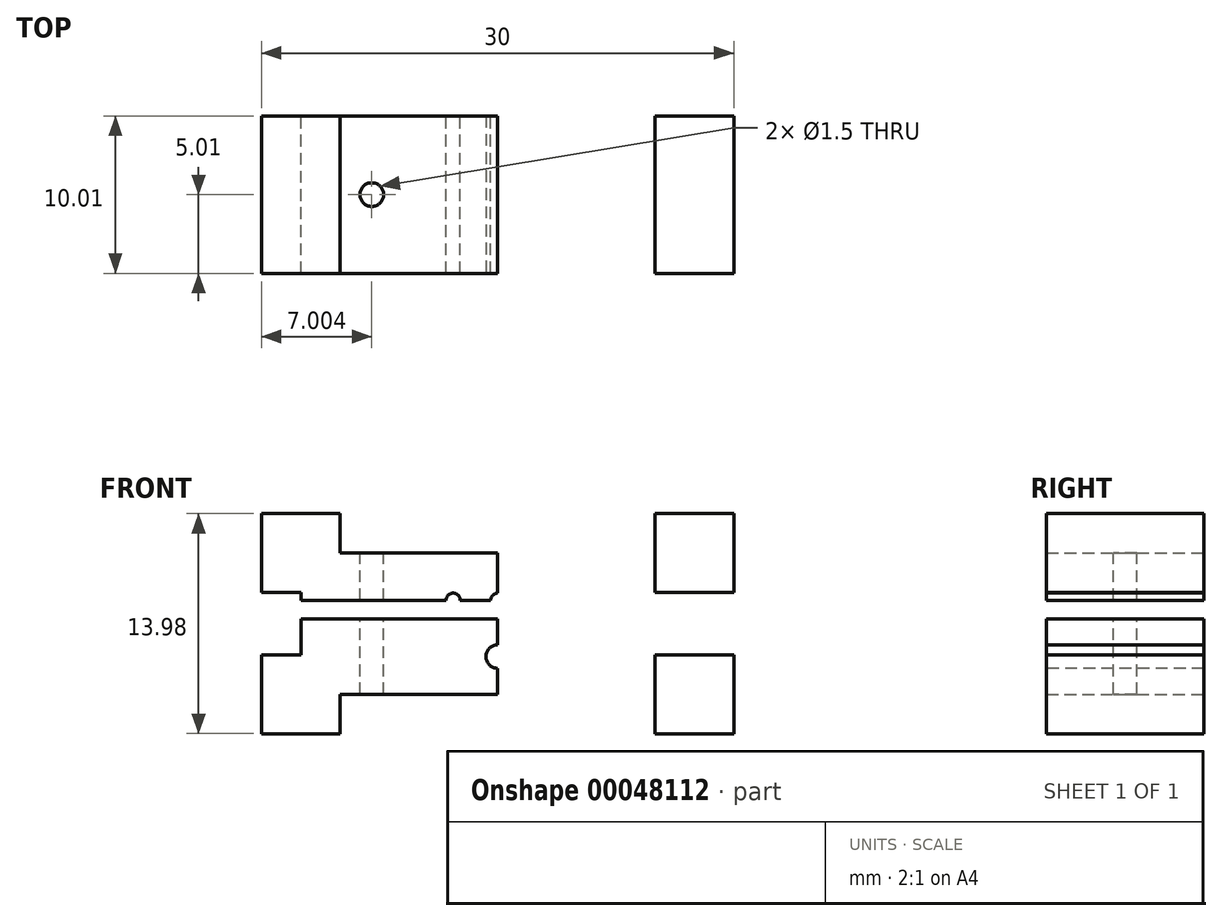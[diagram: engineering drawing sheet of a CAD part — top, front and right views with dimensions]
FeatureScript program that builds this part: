
annotation { "Feature Type Name" : "Feature", "Feature Type Description" : "" }
export const myFeature = defineFeature(function(context is Context, id is Id, definition is map)
    precondition{}
    {
        {
            var Q0;
            Q0=qCreatedBy(makeId("Front.planeOp"),FACE);
            var sketch = newSketch(context, id + "F0", { "sketchPlane" : qUnion([Q0])});
            skLineSegment(sketch, "E0.bottom", {"start": v(-11.09, -0.38) * mm, "end": v(1.41, -0.38) * mm});
            skLineSegment(sketch, "E0.top", {"start": v(-11.09, -5.18) * mm, "end": v(1.41, -5.18) * mm});
            skLineSegment(sketch, "E0.left", {"start": v(-11.09, -0.38) * mm, "end": v(-11.09, -5.18) * mm});
            skLineSegment(sketch, "E0.right", {"start": v(1.41, -0.38) * mm, "end": v(1.41, -5.18) * mm});
            skLineSegment(sketch, "E1.rect.bottom", {"start": v(-8.59, -2.68) * mm, "end": v(-13.59, -2.68) * mm});
            skLineSegment(sketch, "E1.rect.top", {"start": v(-8.59, -7.68) * mm, "end": v(-13.59, -7.68) * mm});
            skLineSegment(sketch, "E1.rect.left", {"start": v(-8.59, -2.68) * mm, "end": v(-8.59, -7.68) * mm});
            skLineSegment(sketch, "E1.rect.right", {"start": v(-13.59, -2.68) * mm, "end": v(-13.59, -7.68) * mm});
            skPoint(sketch, "E1.rect.middle", {"position": v(-11.09, -5.18) * mm});
            skLineSegment(sketch, "E2.bottom", {"start": v(-11.09, 0.8) * mm, "end": v(1.41, 0.8) * mm});
            skLineSegment(sketch, "E2.top", {"start": v(-11.09, 3.8) * mm, "end": v(1.41, 3.8) * mm});
            skLineSegment(sketch, "E2.left", {"start": v(-11.09, 0.8) * mm, "end": v(-11.09, 3.8) * mm});
            skLineSegment(sketch, "E2.right", {"start": v(1.41, 0.8) * mm, "end": v(1.41, 3.8) * mm});
            skLineSegment(sketch, "E3.rect.bottom", {"start": v(-8.59, 6.3) * mm, "end": v(-13.59, 6.3) * mm});
            skLineSegment(sketch, "E3.rect.top", {"start": v(-8.59, 1.3) * mm, "end": v(-13.59, 1.3) * mm});
            skLineSegment(sketch, "E3.rect.left", {"start": v(-8.59, 6.3) * mm, "end": v(-8.59, 1.3) * mm});
            skLineSegment(sketch, "E3.rect.right", {"start": v(-13.59, 6.3) * mm, "end": v(-13.59, 1.3) * mm});
            skPoint(sketch, "E3.rect.middle", {"position": v(-11.09, 3.8) * mm});
            skCircle(sketch, "E4", {"center": v(1.41, 0.8) * mm, "radius": 0.45 * mm});
            skCircle(sketch, "E5.MirrorC", {"center": v(-1.41, 0.8) * mm, "radius": 0.45 * mm});
            skCircle(sketch, "E6.MirrorC", {"center": v(4.24, 0.8) * mm, "radius": 0.45 * mm});
            skPoint(sketch, "E7.MirrorP", {"position": v(13.91, -5.18) * mm});
            skLineSegment(sketch, "E8.MirrorCS", {"start": v(11.41, -7.68) * mm, "end": v(16.41, -7.68) * mm});
            skLineSegment(sketch, "E9.MirrorCS", {"start": v(11.41, -2.68) * mm, "end": v(16.41, -2.68) * mm});
            skLineSegment(sketch, "E10.MirrorCS", {"start": v(11.41, 6.3) * mm, "end": v(11.41, 1.3) * mm});
            skLineSegment(sketch, "E11.MirrorCS", {"start": v(16.41, -2.68) * mm, "end": v(16.41, -7.68) * mm});
            skPoint(sketch, "E12.MirrorP", {"position": v(13.91, 3.8) * mm});
            skLineSegment(sketch, "E13.MirrorCS", {"start": v(11.41, 6.3) * mm, "end": v(16.41, 6.3) * mm});
            skLineSegment(sketch, "E14.MirrorCS", {"start": v(13.91, -0.38) * mm, "end": v(1.41, -0.38) * mm});
            skLineSegment(sketch, "E15.MirrorCS", {"start": v(13.91, -0.38) * mm, "end": v(13.91, -5.18) * mm});
            skLineSegment(sketch, "E16.MirrorCS", {"start": v(13.91, -5.18) * mm, "end": v(1.41, -5.18) * mm});
            skLineSegment(sketch, "E17.MirrorCS", {"start": v(16.41, 6.3) * mm, "end": v(16.41, 1.3) * mm});
            skLineSegment(sketch, "E18.MirrorCS", {"start": v(13.91, 3.8) * mm, "end": v(1.41, 3.8) * mm});
            skLineSegment(sketch, "E19.MirrorCS", {"start": v(13.91, 0.8) * mm, "end": v(1.41, 0.8) * mm});
            skLineSegment(sketch, "E20.MirrorCS", {"start": v(11.41, 1.3) * mm, "end": v(16.41, 1.3) * mm});
            skLineSegment(sketch, "E21.MirrorCS", {"start": v(13.91, 0.8) * mm, "end": v(13.91, 3.8) * mm});
            skLineSegment(sketch, "E22.MirrorCS", {"start": v(11.41, -2.68) * mm, "end": v(11.41, -7.68) * mm});
            skPoint(sketch, "E23", {"position": v(1.41, -2.78) * mm});
            skSolve(sketch);
        }
        {
            var Q0;
            {var subQ0=sQuery(id+"F0.wireOp",EDGE,"E2.left");var subQ1=sQuery(id+"F0.wireOp",EDGE,"E2.bottom");var subQ2=makeQuery(id+"F0.imprint","INTERSECT",VERTEX,{"derivedFrom":[subQ1,subQ0]});Q0=makeQuery(id+"F0.imprint","IMPRINT",FACE,{"disambiguationData":[TD([[makeQuery(id+"F0.imprint","IMPRINT",EDGE,{"disambiguationData":[TD([[subQ2,-1.0]])],"derivedFrom":subQ1}),1.0]])]});}
            var Q1;
            {var subQ6=sQuery(id+"F0.wireOp",EDGE,"E19.MirrorCS");var subQ12=sQuery(id+"F0.wireOp",EDGE,"E4");var subQ13=makeQuery(id+"F0.imprint","INTERSECT",VERTEX,{"derivedFrom":[subQ12,subQ6]});Q1=makeQuery(id+"F0.imprint","IMPRINT",FACE,{"disambiguationData":[TD([[makeQuery(id+"F0.imprint","IMPRINT",EDGE,{"disambiguationData":[TD([[subQ13,1.0]])],"derivedFrom":subQ12}),1.0]])]});}
            var Q2;
            {var subQ0=sQuery(id+"F0.wireOp",EDGE,"E3.rect.bottom");Q2=makeQuery(id+"F0.imprint","IMPRINT",FACE,{"disambiguationData":[TD([[makeQuery(id+"F0.imprint","IMPRINT",EDGE,{"derivedFrom":subQ0}),1.0]])]});}
            var Q3;
            {var subQ0=sQuery(id+"F0.wireOp",EDGE,"E2.left");var subQ1=sQuery(id+"F0.wireOp",EDGE,"E2.top");var subQ2=makeQuery(id+"F0.imprint","INTERSECT",VERTEX,{"derivedFrom":[subQ1,subQ0]});Q3=makeQuery(id+"F0.imprint","IMPRINT",FACE,{"disambiguationData":[TD([[makeQuery(id+"F0.imprint","IMPRINT",EDGE,{"disambiguationData":[TD([[subQ2,-1.0]])],"derivedFrom":subQ1}),-1.0]])]});}
            var Q4;
            {var subQ1=sQuery(id+"F0.wireOp",EDGE,"E13.MirrorCS");Q4=makeQuery(id+"F0.imprint","IMPRINT",FACE,{"disambiguationData":[TD([[makeQuery(id+"F0.imprint","IMPRINT",EDGE,{"derivedFrom":subQ1}),-1.0]])]});}
            var Q5;
            {var subQ0=sQuery(id+"F0.wireOp",EDGE,"E20.MirrorCS");var subQ1=sQuery(id+"F0.wireOp",EDGE,"E10.MirrorCS");var subQ2=makeQuery(id+"F0.imprint","INTERSECT",VERTEX,{"derivedFrom":[subQ1,subQ0]});Q5=makeQuery(id+"F0.imprint","IMPRINT",FACE,{"disambiguationData":[TD([[makeQuery(id+"F0.imprint","IMPRINT",EDGE,{"disambiguationData":[TD([[subQ2,1.0]])],"derivedFrom":subQ1}),1.0]])]});}
            var Q6;
            {var subQ6=sQuery(id+"F0.wireOp",EDGE,"E0.right");Q6=makeQuery(id+"F0.imprint","IMPRINT",FACE,{"disambiguationData":[TD([[makeQuery(id+"F0.imprint","IMPRINT",EDGE,{"derivedFrom":subQ6}),1.0]])]});}
            var Q7;
            {var subQ0=sQuery(id+"F0.wireOp",EDGE,"E22.MirrorCS");var subQ1=sQuery(id+"F0.wireOp",EDGE,"E9.MirrorCS");var subQ2=makeQuery(id+"F0.imprint","INTERSECT",VERTEX,{"derivedFrom":[subQ1,subQ0]});Q7=makeQuery(id+"F0.imprint","IMPRINT",FACE,{"disambiguationData":[TD([[makeQuery(id+"F0.imprint","IMPRINT",EDGE,{"disambiguationData":[TD([[subQ2,-1.0]])],"derivedFrom":subQ1}),-1.0]])]});}
            var Q8;
            {var subQ6=sQuery(id+"F0.wireOp",EDGE,"E8.MirrorCS");Q8=makeQuery(id+"F0.imprint","IMPRINT",FACE,{"disambiguationData":[TD([[makeQuery(id+"F0.imprint","IMPRINT",EDGE,{"derivedFrom":subQ6}),1.0]])]});}
            var Q9;
            {var subQ0=sQuery(id+"F0.wireOp",EDGE,"E1.rect.top");Q9=makeQuery(id+"F0.imprint","IMPRINT",FACE,{"disambiguationData":[TD([[makeQuery(id+"F0.imprint","IMPRINT",EDGE,{"derivedFrom":subQ0}),-1.0]])]});}
            var Q10;
            {var subQ0=sQuery(id+"F0.wireOp",EDGE,"E0.left");var subQ1=sQuery(id+"F0.wireOp",EDGE,"E0.top");var subQ2=makeQuery(id+"F0.imprint","INTERSECT",VERTEX,{"derivedFrom":[subQ1,subQ0]});Q10=makeQuery(id+"F0.imprint","IMPRINT",FACE,{"disambiguationData":[TD([[makeQuery(id+"F0.imprint","IMPRINT",EDGE,{"disambiguationData":[TD([[subQ2,-1.0]])],"derivedFrom":subQ1}),1.0]])]});}
            var Q11;
            {var subQ5=sQuery(id+"F0.wireOp",EDGE,"E0.bottom");Q11=makeQuery(id+"F0.imprint","IMPRINT",FACE,{"disambiguationData":[TD([[makeQuery(id+"F0.imprint","IMPRINT",EDGE,{"derivedFrom":subQ5}),-1.0]])]});}
            extrude(context, id + "F1", {"entities" : qUnion([Q0, Q1, Q2, Q3, Q4, Q5, Q6, Q7, Q8, Q9, Q10, Q11]), "depth" : 10 * mm});
        }
        {
            var Q0;
            Q0=makeQuery(id+"F1.opExtrude","SWEPT_FACE",FACE,{"disambiguationData":[OSD([sQuery(id+"F0.wireOp",EDGE,"E2.top"),sQuery(id+"F0.wireOp",EDGE,"E18.MirrorCS")])]});
            var sketch = newSketch(context, id + "F2", { "sketchPlane" : qUnion([Q0])});
            skCircle(sketch, "E24", {"center": v(-6.59, -5) * mm, "radius": 2 * mm});
            skCircle(sketch, "E25", {"center": v(9.41, -5) * mm, "radius": 2 * mm});
            skCircle(sketch, "E26", {"center": v(-6.59, -5) * mm, "radius": 0.75 * mm});
            skCircle(sketch, "E27", {"center": v(9.41, -5) * mm, "radius": 0.75 * mm});
            skSolve(sketch);
        }
        {
            var Q0;
            Q0=makeQuery(id+"F2.imprint","IMPRINT",FACE,{"disambiguationData":[TD([[makeQuery(id+"F2.imprint","IMPRINT",EDGE,{"derivedFrom":sQuery(id+"F2.wireOp",EDGE,"E26")}),1.0]])]});
            var Q1;
            Q1=makeQuery(id+"F2.imprint","IMPRINT",FACE,{"disambiguationData":[TD([[makeQuery(id+"F2.imprint","IMPRINT",EDGE,{"derivedFrom":sQuery(id+"F2.wireOp",EDGE,"E27")}),1.0]])]});
            extrude(context, id + "F3", {"entities" : qUnion([Q0, Q1]), "operationType" : NewBodyOperationType.REMOVE, "oppositeDirection" : true, "depth" : 25 * mm});
        }
        {
            var Q0;
            Q0=sQuery(id+"F0.wireOp",VERTEX,"E23");
            var Q1;
            Q1=makeQuery(id+"F1.opExtrude","SWEPT_BODY",BODY,{"disambiguationData":[OSD([sQuery(id+"F0.wireOp",EDGE,"E0.bottom"),sQuery(id+"F0.wireOp",EDGE,"E0.top"),sQuery(id+"F0.wireOp",EDGE,"E0.left"),sQuery(id+"F0.wireOp",EDGE,"E1.rect.bottom"),sQuery(id+"F0.wireOp",EDGE,"E1.rect.top"),sQuery(id+"F0.wireOp",EDGE,"E1.rect.left"),sQuery(id+"F0.wireOp",EDGE,"E1.rect.right"),sQuery(id+"F0.wireOp",EDGE,"E8.MirrorCS"),sQuery(id+"F0.wireOp",EDGE,"E9.MirrorCS"),sQuery(id+"F0.wireOp",EDGE,"E11.MirrorCS"),sQuery(id+"F0.wireOp",EDGE,"E14.MirrorCS"),sQuery(id+"F0.wireOp",EDGE,"E15.MirrorCS"),sQuery(id+"F0.wireOp",EDGE,"E16.MirrorCS"),sQuery(id+"F0.wireOp",EDGE,"E22.MirrorCS")])]});
            hole(context, id + "F4", {"style" : HoleStyle.SIMPLE, "holeDiameter" : 1.5 * mm, "endStyle" : HoleEndStyle.THROUGH, "oppositeDirection" : true, "locations" : qUnion([Q0]), "scope" : qUnion([Q1])});
        }
    });
